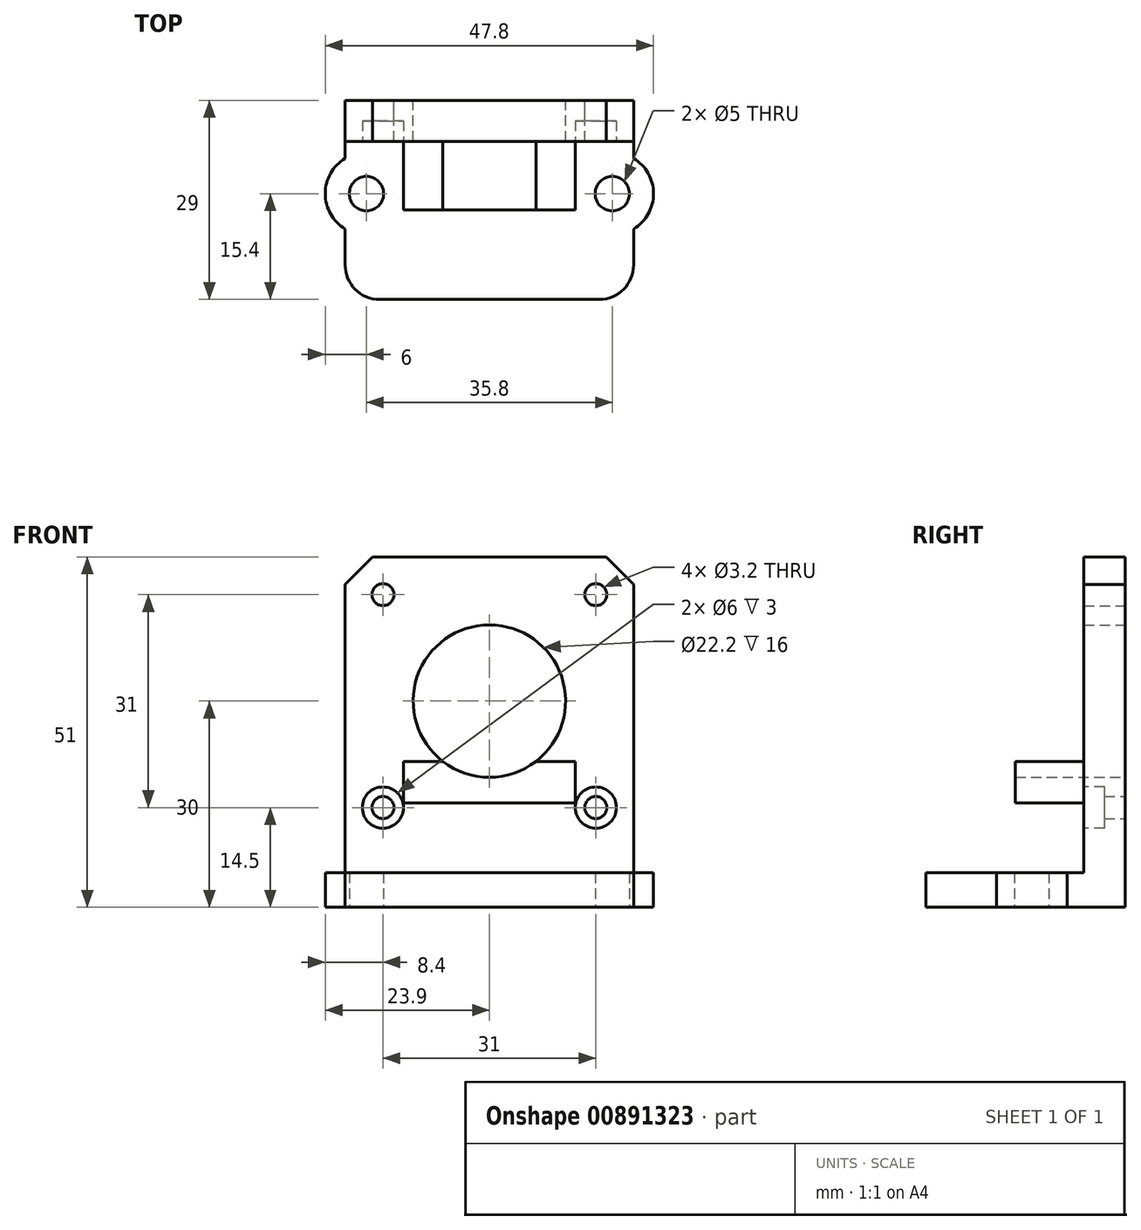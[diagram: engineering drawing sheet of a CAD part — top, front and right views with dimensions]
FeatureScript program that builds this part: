
annotation { "Feature Type Name" : "Feature", "Feature Type Description" : "" }
export const myFeature = defineFeature(function(context is Context, id is Id, definition is map)
    precondition{}
    {
        {
            var Q0;
            Q0=qCreatedBy(makeId("Front.planeOp"),FACE);
            var sketch = newSketch(context, id + "F0", { "sketchPlane" : qUnion([Q0])});
            skLineSegment(sketch, "E0.bottom", {"start": v(0, 0) * mm, "end": v(42, 0) * mm});
            skLineSegment(sketch, "E0.top", {"start": v(0, 51) * mm, "end": v(42, 51) * mm});
            skLineSegment(sketch, "E0.left", {"start": v(0, 0) * mm, "end": v(0, 51) * mm});
            skLineSegment(sketch, "E0.right", {"start": v(42, 0) * mm, "end": v(42, 51) * mm});
            skCircle(sketch, "E1", {"center": v(21, 30) * mm, "radius": 11.1 * mm});
            skSolve(sketch);
        }
        {
            var Q0;
            Q0=makeQuery(id+"F0.imprint","IMPRINT",FACE,{"disambiguationData":[TD([[makeQuery(id+"F0.imprint","IMPRINT",EDGE,{"derivedFrom":sQuery(id+"F0.wireOp",EDGE,"E0.bottom")}),1.0]])]});
            extrude(context, id + "F1", {"entities" : qUnion([Q0]), "depth" : 6 * mm, "offsetDistance" : 25 * mm});
        }
        {
            var Q0;
            Q0=makeQuery(id+"F1.opExtrude","SWEPT_EDGE",EDGE,{"disambiguationData":[OSD([sQuery(id+"F0.wireOp",EDGE,"E0.top"),sQuery(id+"F0.wireOp",EDGE,"E0.left")])]});
            var Q1;
            Q1=makeQuery(id+"F1.opExtrude","SWEPT_EDGE",EDGE,{"disambiguationData":[OSD([sQuery(id+"F0.wireOp",EDGE,"E0.top"),sQuery(id+"F0.wireOp",EDGE,"E0.right")])]});
            chamfer(context, id + "F2", {"entities" : qUnion([Q0, Q1]), "width" : 4 * mm, "tangentPropagation" : true});
        }
        {
            var Q0;
            Q0=makeQuery(id+"F1.opExtrude","CAP_FACE",FACE,{"disambiguationData":[OSD([sQuery(id+"F0.wireOp",EDGE,"E0.bottom"),sQuery(id+"F0.wireOp",EDGE,"E0.top"),sQuery(id+"F0.wireOp",EDGE,"E0.left"),sQuery(id+"F0.wireOp",EDGE,"E0.right"),sQuery(id+"F0.wireOp",EDGE,"E1")])],"isStart":false});
            var sketch = newSketch(context, id + "F3", { "sketchPlane" : qUnion([Q0])});
            skLineSegment(sketch, "E2.bottom", {"start": v(0, 0) * mm, "end": v(42, 0) * mm});
            skLineSegment(sketch, "E2.top", {"start": v(0, 5) * mm, "end": v(42, 5) * mm});
            skLineSegment(sketch, "E2.left", {"start": v(0, 0) * mm, "end": v(0, 5) * mm});
            skLineSegment(sketch, "E2.right", {"start": v(42, 0) * mm, "end": v(42, 5) * mm});
            skSolve(sketch);
        }
        {
            var Q0;
            Q0=makeQuery(id+"F3.imprint","IMPRINT",FACE,{"disambiguationData":[TD([[makeQuery(id+"F3.imprint","IMPRINT",EDGE,{"derivedFrom":sQuery(id+"F3.wireOp",EDGE,"E2.bottom")}),1.0]])]});
            extrude(context, id + "F4", {"entities" : qUnion([Q0]), "operationType" : NewBodyOperationType.ADD, "depth" : 23 * mm, "offsetDistance" : 25 * mm});
        }
        {
            var Q0;
            Q0=makeQuery(id+"F1.opExtrude","CAP_FACE",FACE,{"disambiguationData":[OSD([sQuery(id+"F0.wireOp",EDGE,"E0.bottom"),sQuery(id+"F0.wireOp",EDGE,"E0.top"),sQuery(id+"F0.wireOp",EDGE,"E0.left"),sQuery(id+"F0.wireOp",EDGE,"E0.right"),sQuery(id+"F0.wireOp",EDGE,"E1")])],"isStart":false});
            var sketch = newSketch(context, id + "F5", { "sketchPlane" : qUnion([Q0])});
            skLineSegment(sketch, "E3.bottom", {"start": v(8.5, 21.2) * mm, "end": v(33.5, 21.2) * mm});
            skLineSegment(sketch, "E3.top", {"start": v(8.5, 15.2) * mm, "end": v(33.5, 15.2) * mm});
            skLineSegment(sketch, "E3.left", {"start": v(8.5, 21.2) * mm, "end": v(8.5, 15.2) * mm});
            skLineSegment(sketch, "E3.right", {"start": v(33.5, 21.2) * mm, "end": v(33.5, 15.2) * mm});
            skSolve(sketch);
        }
        {
            var Q0;
            Q0=makeQuery(id+"F5.imprint","IMPRINT",FACE,{"disambiguationData":[TD([[makeQuery(id+"F5.imprint","IMPRINT",EDGE,{"derivedFrom":sQuery(id+"F5.wireOp",EDGE,"E3.top")}),1.0]])]});
            extrude(context, id + "F6", {"entities" : qUnion([Q0]), "operationType" : NewBodyOperationType.ADD, "depth" : 10 * mm, "offsetDistance" : 25 * mm});
        }
        {
            var Q0;
            Q0=makeQuery(id+"F1.opExtrude","CAP_FACE",FACE,{"disambiguationData":[OSD([sQuery(id+"F0.wireOp",EDGE,"E0.bottom"),sQuery(id+"F0.wireOp",EDGE,"E0.top"),sQuery(id+"F0.wireOp",EDGE,"E0.left"),sQuery(id+"F0.wireOp",EDGE,"E0.right"),sQuery(id+"F0.wireOp",EDGE,"E1")])],"isStart":true});
            var sketch = newSketch(context, id + "F7", { "sketchPlane" : qUnion([Q0])});
            skCircle(sketch, "E4", {"center": v(-36.5, 45.5) * mm, "radius": 1.6 * mm});
            skCircle(sketch, "E5", {"center": v(-21, 30) * mm, "radius": 5.7 * mm});
            skCircle(sketch, "E6.0.1.0", {"center": v(-36.5, 14.5) * mm, "radius": 1.6 * mm});
            skCircle(sketch, "E6.1.0.0", {"center": v(-5.5, 45.5) * mm, "radius": 1.6 * mm});
            skCircle(sketch, "E6.1.1.0", {"center": v(-5.5, 14.5) * mm, "radius": 1.6 * mm});
            skLineSegment(sketch, "E6.direction1", {"start": v(-36.5, 45.5) * mm, "end": v(-5.5, 45.5) * mm, "construction": true});
            skLineSegment(sketch, "E6.direction2", {"start": v(-36.5, 45.5) * mm, "end": v(-36.5, 14.5) * mm, "construction": true});
            skSolve(sketch);
        }
        {
            var Q0;
            Q0=makeQuery(id+"F7.imprint","IMPRINT",FACE,{"disambiguationData":[TD([[makeQuery(id+"F7.imprint","IMPRINT",EDGE,{"derivedFrom":sQuery(id+"F7.wireOp",EDGE,"E4")}),1.0]])]});
            var Q1;
            Q1=makeQuery(id+"F7.imprint","IMPRINT",FACE,{"disambiguationData":[TD([[makeQuery(id+"F7.imprint","IMPRINT",EDGE,{"derivedFrom":sQuery(id+"F7.wireOp",EDGE,"E6.1.0.0")}),1.0]])]});
            var Q2;
            Q2=makeQuery(id+"F7.imprint","IMPRINT",FACE,{"disambiguationData":[TD([[makeQuery(id+"F7.imprint","IMPRINT",EDGE,{"derivedFrom":sQuery(id+"F7.wireOp",EDGE,"E6.1.1.0")}),1.0]])]});
            var Q3;
            Q3=makeQuery(id+"F7.imprint","IMPRINT",FACE,{"disambiguationData":[TD([[makeQuery(id+"F7.imprint","IMPRINT",EDGE,{"derivedFrom":sQuery(id+"F7.wireOp",EDGE,"E6.0.1.0")}),1.0]])]});
            extrude(context, id + "F8", {"entities" : qUnion([Q0, Q1, Q2, Q3]), "operationType" : NewBodyOperationType.REMOVE, "oppositeDirection" : true, "depth" : 25 * mm, "offsetDistance" : 25 * mm});
        }
        {
            var Q0;
            Q0=qCreatedBy(makeId("Top.planeOp"),FACE);
            var sketch = newSketch(context, id + "F9", { "sketchPlane" : qUnion([Q0])});
            skCircle(sketch, "E7", {"center": v(3.1, -13.6) * mm, "radius": 2.5 * mm});
            skCircle(sketch, "E8", {"center": v(38.9, -13.6) * mm, "radius": 2.5 * mm});
            skSolve(sketch);
        }
        {
            var Q0;
            Q0=makeQuery(id+"F9.imprint","IMPRINT",FACE,{"disambiguationData":[TD([[makeQuery(id+"F9.imprint","IMPRINT",EDGE,{"derivedFrom":sQuery(id+"F9.wireOp",EDGE,"E7")}),1.0]])]});
            var Q1;
            Q1=makeQuery(id+"F9.imprint","IMPRINT",FACE,{"disambiguationData":[TD([[makeQuery(id+"F9.imprint","IMPRINT",EDGE,{"derivedFrom":sQuery(id+"F9.wireOp",EDGE,"E8")}),1.0]])]});
            extrude(context, id + "F10", {"entities" : qUnion([Q0, Q1]), "operationType" : NewBodyOperationType.REMOVE, "depth" : 6 * mm, "offsetDistance" : 25 * mm});
        }
        {
            var Q0;
            Q0=makeQuery(id+"F1.opExtrude","CAP_FACE",FACE,{"disambiguationData":[OSD([sQuery(id+"F0.wireOp",EDGE,"E0.bottom"),sQuery(id+"F0.wireOp",EDGE,"E0.top"),sQuery(id+"F0.wireOp",EDGE,"E0.left"),sQuery(id+"F0.wireOp",EDGE,"E0.right"),sQuery(id+"F0.wireOp",EDGE,"E1")])],"isStart":false});
            var sketch = newSketch(context, id + "F11", { "sketchPlane" : qUnion([Q0])});
            skCircle(sketch, "E9", {"center": v(5.5, 14.5) * mm, "radius": 3 * mm});
            skCircle(sketch, "E10", {"center": v(36.5, 14.5) * mm, "radius": 3 * mm});
            skSolve(sketch);
        }
        {
            var Q0;
            Q0 = qSketchRegion(id + "F11", true);
            extrude(context, id + "F12", {"entities" : qUnion([Q0]), "operationType" : NewBodyOperationType.REMOVE, "oppositeDirection" : true, "depth" : 3 * mm, "offsetDistance" : 25 * mm});
        }
        {
            var Q0;
            Q0=makeQuery(id+"F4.opExtrude","SWEPT_FACE",FACE,{"disambiguationData":[OSD([sQuery(id+"F3.wireOp",EDGE,"E2.top")])]});
            var sketch = newSketch(context, id + "F13", { "sketchPlane" : qUnion([Q0])});
            skCircle(sketch, "E11", {"center": v(3.1, -13.6) * mm, "radius": 6 * mm});
            skCircle(sketch, "E12", {"center": v(38.9, -13.6) * mm, "radius": 6 * mm});
            skSolve(sketch);
        }
        {
            var Q0;
            {var subQ0=sQuery(id+"F13.wireOp",EDGE,"E11");var subQ1=makeQuery(id+"F4.opExtrude","SWEPT_EDGE",EDGE,{"disambiguationData":[OSD([sQuery(id+"F0.wireOp",EDGE,"E0.left"),sQuery(id+"F3.wireOp",EDGE,"E2.top"),sQuery(id+"F3.wireOp",EDGE,"E2.left")])]});var subQ2=makeQuery(id+"F13.imprint","INTERSECT",VERTEX,{"disambiguationData":[OD(0.0)],"derivedFrom":[subQ1,subQ0]});Q0=makeQuery(id+"F13.imprint","IMPRINT",FACE,{"disambiguationData":[TD([[makeQuery(id+"F13.imprint","IMPRINT",EDGE,{"disambiguationData":[TD([[subQ2,1.0]])],"derivedFrom":subQ0}),1.0]])]});}
            var Q1;
            {var subQ0=sQuery(id+"F13.wireOp",EDGE,"E12");var subQ1=makeQuery(id+"F4.opExtrude","SWEPT_EDGE",EDGE,{"disambiguationData":[OSD([sQuery(id+"F0.wireOp",EDGE,"E0.right"),sQuery(id+"F3.wireOp",EDGE,"E2.top"),sQuery(id+"F3.wireOp",EDGE,"E2.right")])]});var subQ2=makeQuery(id+"F13.imprint","INTERSECT",VERTEX,{"disambiguationData":[OD(0.0)],"derivedFrom":[subQ1,subQ0]});Q1=makeQuery(id+"F13.imprint","IMPRINT",FACE,{"disambiguationData":[TD([[makeQuery(id+"F13.imprint","IMPRINT",EDGE,{"disambiguationData":[TD([[subQ2,-1.0]])],"derivedFrom":subQ0}),1.0]])]});}
            extrude(context, id + "F14", {"entities" : qUnion([Q0, Q1]), "operationType" : NewBodyOperationType.ADD, "oppositeDirection" : true, "depth" : 5 * mm, "offsetDistance" : 25 * mm});
        }
        {
            var Q0;
            Q0=makeQuery(id+"F4.opExtrude","CAP_EDGE",EDGE,{"disambiguationData":[OSD([sQuery(id+"F3.wireOp",EDGE,"E2.left")])],"isStart":false});
            var Q1;
            Q1=makeQuery(id+"F4.opExtrude","CAP_EDGE",EDGE,{"disambiguationData":[OSD([sQuery(id+"F3.wireOp",EDGE,"E2.right")])],"isStart":false});
            fillet(context, id + "F15", {"entities" : qUnion([Q0, Q1]), "radius" : 5 * mm, "tangentPropagation" : true, "allowEdgeOverflow" : false});
        }
    });
